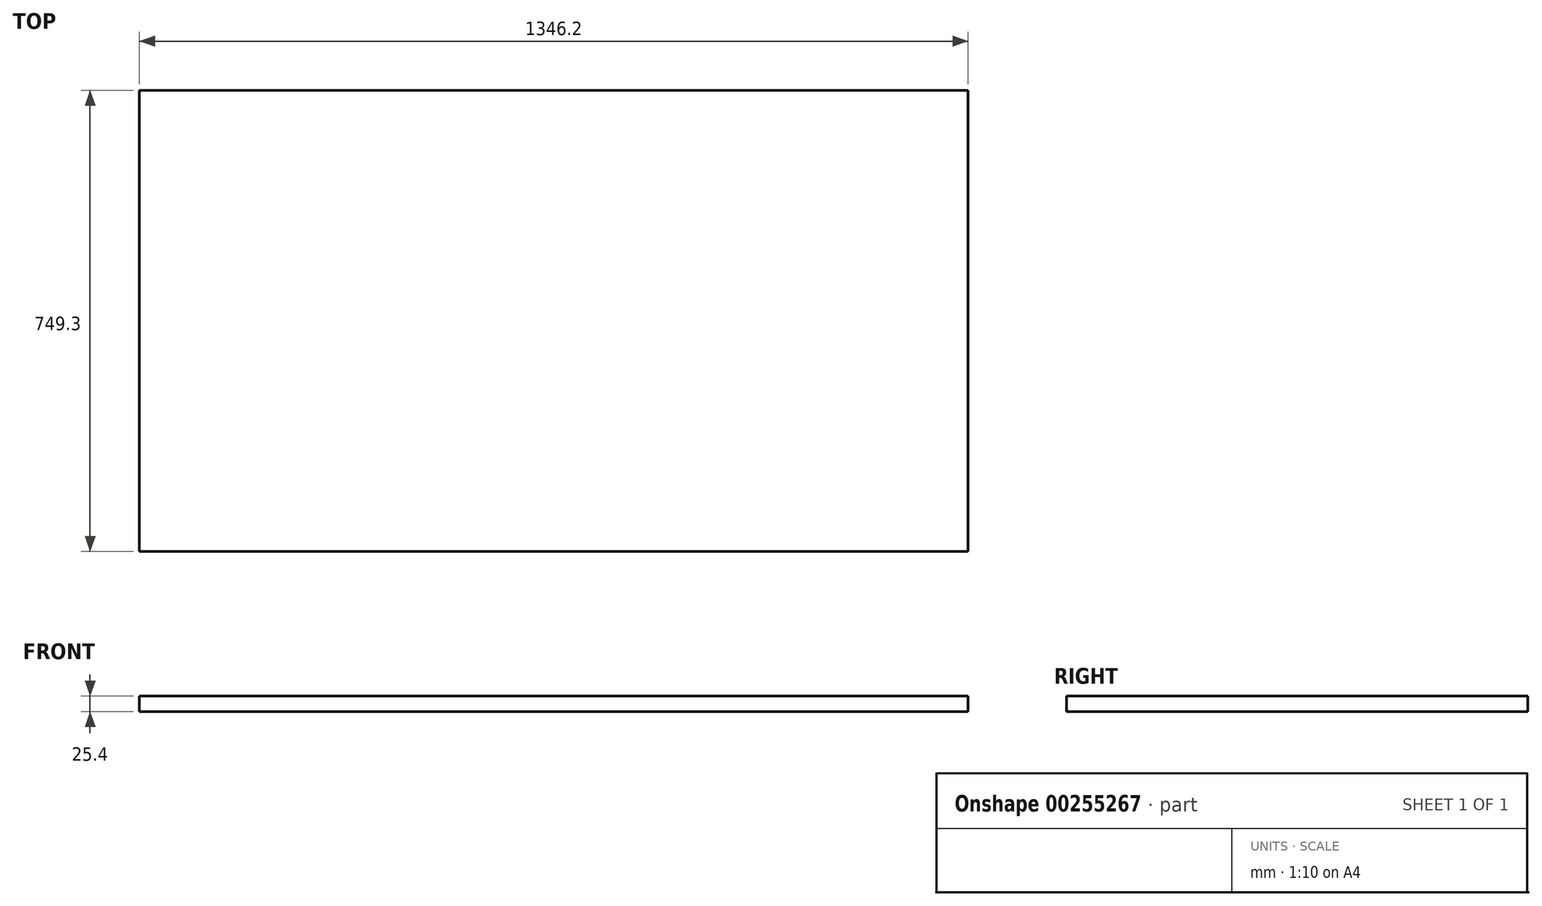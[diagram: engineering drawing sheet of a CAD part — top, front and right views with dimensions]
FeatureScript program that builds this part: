
annotation { "Feature Type Name" : "Feature", "Feature Type Description" : "" }
export const myFeature = defineFeature(function(context is Context, id is Id, definition is map)
    precondition{}
    {
        {
            var Q0;
            Q0=qCreatedBy(makeId("Top.planeOp"),FACE);
            var sketch = newSketch(context, id + "F1", { "sketchPlane" : qUnion([Q0])});
            skLineSegment(sketch, "E0.bottom", {"start": v(673.1, 374.65) * mm, "end": v(-673.1, 374.65) * mm});
            skLineSegment(sketch, "E0.top", {"start": v(673.1, -374.65) * mm, "end": v(-673.1, -374.65) * mm});
            skLineSegment(sketch, "E0.left", {"start": v(673.1, 374.65) * mm, "end": v(673.1, -374.65) * mm});
            skLineSegment(sketch, "E0.right", {"start": v(-673.1, 374.65) * mm, "end": v(-673.1, -374.65) * mm});
            skPoint(sketch, "E0.middle", {"position": v(0, 0) * mm});
            skSolve(sketch);
        }
        {
            var Q0;
            Q0 = qSketchRegion(id + "F1", true);
            extrude(context, id + "F0", {"entities" : qUnion([Q0]), "depth" : 25.4 * mm});
        }
    });
